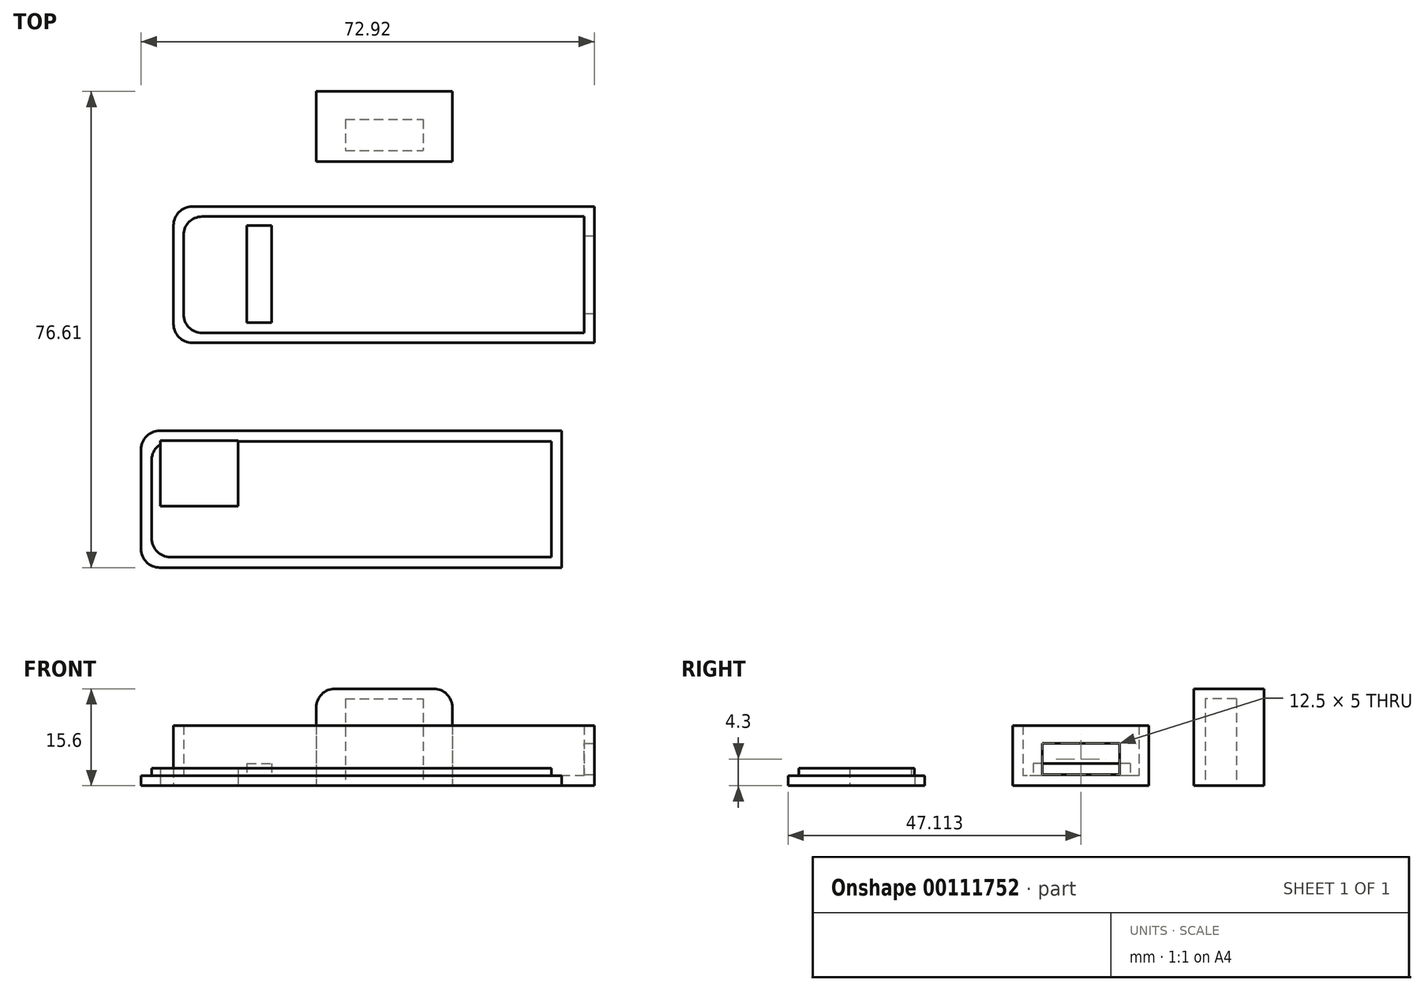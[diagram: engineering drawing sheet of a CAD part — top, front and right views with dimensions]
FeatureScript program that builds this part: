
annotation { "Feature Type Name" : "Feature", "Feature Type Description" : "" }
export const myFeature = defineFeature(function(context is Context, id is Id, definition is map)
    precondition{}
    {
        {
            var Q0;
            Q0=qCreatedBy(makeId("Top.planeOp"),FACE);
            var sketch = newSketch(context, id + "F0", { "sketchPlane" : qUnion([Q0])});
            skLineSegment(sketch, "E0.bottom", {"start": v(32.32, 10.9) * mm, "end": v(-29.18, 10.9) * mm});
            skLineSegment(sketch, "E0.top", {"start": v(32.32, -7.8) * mm, "end": v(-29.18, -7.8) * mm});
            skLineSegment(sketch, "E0.left", {"start": v(32.32, 10.9) * mm, "end": v(32.32, -7.8) * mm});
            skLineSegment(sketch, "E0.right", {"start": v(-32.18, 7.9) * mm, "end": v(-32.18, -4.8) * mm});
            skLineSegment(sketch, "E1.0", {"start": v(33.92, 12.5) * mm, "end": v(-30.78, 12.5) * mm});
            skLineSegment(sketch, "E1.1", {"start": v(33.92, 12.5) * mm, "end": v(33.92, -9.4) * mm});
            skLineSegment(sketch, "E1.2", {"start": v(33.92, -9.4) * mm, "end": v(-30.78, -9.4) * mm});
            skLineSegment(sketch, "E1.3", {"start": v(-33.78, 9.5) * mm, "end": v(-33.78, -6.4) * mm});
            skPoint(sketch, "E2.visualSharp", {"position": v(-32.18, 10.9) * mm});
            skArc(sketch, "E2.filletArc", {"start": v(-29.18, 10.9) * mm, "mid": v(-31.3, 10.02) * mm, "end": v(-32.18, 7.9) * mm});
            skPoint(sketch, "E3.visualSharp", {"position": v(-32.18, -7.8) * mm});
            skArc(sketch, "E3.filletArc", {"start": v(-32.18, -4.8) * mm, "mid": v(-31.3, -6.92) * mm, "end": v(-29.18, -7.8) * mm});
            skPoint(sketch, "E4.visualSharp", {"position": v(-33.78, -9.4) * mm});
            skArc(sketch, "E4.filletArc", {"start": v(-33.78, -6.4) * mm, "mid": v(-32.9, -8.52) * mm, "end": v(-30.78, -9.4) * mm});
            skPoint(sketch, "E5.visualSharp", {"position": v(-33.78, 12.5) * mm});
            skArc(sketch, "E5.filletArc", {"start": v(-30.78, 12.5) * mm, "mid": v(-32.9, 11.62) * mm, "end": v(-33.78, 9.5) * mm});
            skSolve(sketch);
        }
        {
            var Q0;
            Q0=makeQuery(id+"F0.imprint","IMPRINT",FACE,{"disambiguationData":[TD([[makeQuery(id+"F0.imprint","IMPRINT",EDGE,{"derivedFrom":sQuery(id+"F0.wireOp",EDGE,"E0.bottom")}),-1.0]])]});
            extrude(context, id + "F1", {"entities" : qUnion([Q0]), "depth" : (10.5 - 0.8) * mm});
        }
        {
            var Q0;
            Q0=makeQuery(id+"F0.imprint","IMPRINT",FACE,{"disambiguationData":[TD([[makeQuery(id+"F0.imprint","IMPRINT",EDGE,{"derivedFrom":sQuery(id+"F0.wireOp",EDGE,"E0.bottom")}),1.0]])]});
            extrude(context, id + "F2", {"entities" : qUnion([Q0]), "operationType" : NewBodyOperationType.ADD, "depth" : 1.6 * mm});
        }
        {
            var Q0;
            Q0=makeQuery(id+"F1.opExtrude","SWEPT_FACE",FACE,{"disambiguationData":[OSD([sQuery(id+"F0.wireOp",EDGE,"E1.1")])]});
            var sketch = newSketch(context, id + "F3", { "sketchPlane" : qUnion([Q0])});
            skLineSegment(sketch, "E6.bottom", {"start": v(-4.7, 6.8) * mm, "end": v(7.8, 6.8) * mm});
            skLineSegment(sketch, "E6.top", {"start": v(-4.7, 1.8) * mm, "end": v(7.8, 1.8) * mm});
            skLineSegment(sketch, "E6.left", {"start": v(-4.7, 6.8) * mm, "end": v(-4.7, 1.8) * mm});
            skLineSegment(sketch, "E6.right", {"start": v(7.8, 6.8) * mm, "end": v(7.8, 1.8) * mm});
            skSolve(sketch);
        }
        {
            var Q0;
            Q0=makeQuery(id+"F3.imprint","IMPRINT",FACE,{"disambiguationData":[TD([[makeQuery(id+"F3.imprint","IMPRINT",EDGE,{"derivedFrom":sQuery(id+"F3.wireOp",EDGE,"E6.bottom")}),-1.0]])]});
            extrude(context, id + "F4", {"entities" : qUnion([Q0]), "operationType" : NewBodyOperationType.REMOVE, "endBound" : BoundingType.UP_TO_NEXT, "oppositeDirection" : true, "depth" : 25 * mm});
        }
        {
            var Q0;
            Q0=makeQuery(id+"F2.opExtrude","CAP_FACE",FACE,{"disambiguationData":[OSD([sQuery(id+"F0.wireOp",EDGE,"E0.bottom"),sQuery(id+"F0.wireOp",EDGE,"E0.top"),sQuery(id+"F0.wireOp",EDGE,"E0.left"),sQuery(id+"F0.wireOp",EDGE,"E0.right")])],"isStart":false});
            var sketch = newSketch(context, id + "F5", { "sketchPlane" : qUnion([Q0])});
            skLineSegment(sketch, "E7.bottom", {"start": v(-21.98, 9.49) * mm, "end": v(-18, 9.49) * mm});
            skLineSegment(sketch, "E7.top", {"start": v(-21.98, -6.15) * mm, "end": v(-18, -6.15) * mm});
            skLineSegment(sketch, "E7.left", {"start": v(-21.98, 9.49) * mm, "end": v(-21.98, -6.15) * mm});
            skLineSegment(sketch, "E7.right", {"start": v(-18, 9.49) * mm, "end": v(-18, -6.15) * mm});
            skSolve(sketch);
        }
        {
            var Q0;
            Q0 = qSketchRegion(id + "F5", true);
            extrude(context, id + "F6", {"entities" : qUnion([Q0]), "operationType" : NewBodyOperationType.ADD, "depth" : 2 * mm});
        }
        {
            var Q0;
            Q0=qCreatedBy(makeId("Top.planeOp"),FACE);
            var sketch = newSketch(context, id + "F7", { "sketchPlane" : qUnion([Q0])});
            skLineSegment(sketch, "E8.bottom", {"start": v(28.7, -23.56) * mm, "end": v(-36, -23.56) * mm});
            skLineSegment(sketch, "E8.top", {"start": v(28.7, -45.56) * mm, "end": v(-36, -45.56) * mm});
            skLineSegment(sketch, "E8.left", {"start": v(28.7, -23.56) * mm, "end": v(28.7, -45.56) * mm});
            skLineSegment(sketch, "E8.right", {"start": v(-39, -26.56) * mm, "end": v(-39, -42.56) * mm});
            skPoint(sketch, "E9.visualSharp", {"position": v(-39, -23.56) * mm});
            skArc(sketch, "E9.filletArc", {"start": v(-36, -23.56) * mm, "mid": v(-38.13, -24.44) * mm, "end": v(-39, -26.56) * mm});
            skPoint(sketch, "E10.visualSharp", {"position": v(-39, -45.56) * mm});
            skArc(sketch, "E10.filletArc", {"start": v(-39, -42.56) * mm, "mid": v(-38.13, -44.68) * mm, "end": v(-36, -45.56) * mm});
            skLineSegment(sketch, "E11.0", {"start": v(-37.3, -28.26) * mm, "end": v(-37.3, -40.86) * mm});
            skLineSegment(sketch, "E11.1", {"start": v(27, -25.26) * mm, "end": v(-34.3, -25.26) * mm});
            skLineSegment(sketch, "E11.2", {"start": v(27, -25.26) * mm, "end": v(27, -43.86) * mm});
            skLineSegment(sketch, "E11.3", {"start": v(27, -43.86) * mm, "end": v(-34.3, -43.86) * mm});
            skPoint(sketch, "E12.visualSharp", {"position": v(-37.3, -25.26) * mm});
            skArc(sketch, "E12.filletArc", {"start": v(-34.3, -25.26) * mm, "mid": v(-36.43, -26.14) * mm, "end": v(-37.3, -28.26) * mm});
            skPoint(sketch, "E13.visualSharp", {"position": v(-37.3, -43.86) * mm});
            skArc(sketch, "E13.filletArc", {"start": v(-37.3, -40.86) * mm, "mid": v(-36.43, -42.98) * mm, "end": v(-34.3, -43.86) * mm});
            skSolve(sketch);
        }
        {
            var Q0;
            Q0=makeQuery(id+"F7.imprint","IMPRINT",FACE,{"disambiguationData":[TD([[makeQuery(id+"F7.imprint","IMPRINT",EDGE,{"derivedFrom":sQuery(id+"F7.wireOp",EDGE,"E11.0")}),1.0]])]});
            var Q1;
            Q1=makeQuery(id+"F7.imprint","IMPRINT",FACE,{"disambiguationData":[TD([[makeQuery(id+"F7.imprint","IMPRINT",EDGE,{"derivedFrom":sQuery(id+"F7.wireOp",EDGE,"E8.bottom")}),1.0]])]});
            extrude(context, id + "F8", {"entities" : qUnion([Q0, Q1]), "depth" : 1.6 * mm});
        }
        {
            var Q0;
            Q0=makeQuery(id+"F7.imprint","IMPRINT",FACE,{"disambiguationData":[TD([[makeQuery(id+"F7.imprint","IMPRINT",EDGE,{"derivedFrom":sQuery(id+"F7.wireOp",EDGE,"E11.0")}),1.0]])]});
            extrude(context, id + "F9", {"entities" : qUnion([Q0]), "operationType" : NewBodyOperationType.ADD, "depth" : (1.6 + 1.2) * mm});
        }
        {
            var Q0;
            Q0=makeQuery(id+"F8.opExtrude","CAP_FACE",FACE,{"disambiguationData":[OSD([sQuery(id+"F7.wireOp",EDGE,"E8.bottom"),sQuery(id+"F7.wireOp",EDGE,"E8.top"),sQuery(id+"F7.wireOp",EDGE,"E8.left"),sQuery(id+"F7.wireOp",EDGE,"E8.right"),sQuery(id+"F7.wireOp",EDGE,"E9.filletArc"),sQuery(id+"F7.wireOp",EDGE,"E10.filletArc")])],"isStart":true});
            var sketch = newSketch(context, id + "F10", { "sketchPlane" : qUnion([Q0])});
            skLineSegment(sketch, "E14.bottom", {"start": v(-35.9, 35.66) * mm, "end": v(-23.4, 35.66) * mm});
            skLineSegment(sketch, "E14.top", {"start": v(-35.9, 25.16) * mm, "end": v(-23.4, 25.16) * mm});
            skLineSegment(sketch, "E14.left", {"start": v(-35.9, 35.66) * mm, "end": v(-35.9, 25.16) * mm});
            skLineSegment(sketch, "E14.right", {"start": v(-23.4, 35.66) * mm, "end": v(-23.4, 25.16) * mm});
            skSolve(sketch);
        }
        {
            var Q0;
            Q0=makeQuery(id+"F10.imprint","IMPRINT",FACE,{"disambiguationData":[TD([[makeQuery(id+"F10.imprint","IMPRINT",EDGE,{"derivedFrom":sQuery(id+"F10.wireOp",EDGE,"E14.bottom")}),-1.0]])]});
            extrude(context, id + "F11", {"entities" : qUnion([Q0]), "operationType" : NewBodyOperationType.REMOVE, "endBound" : BoundingType.THROUGH_ALL, "oppositeDirection" : true, "depth" : 25 * mm});
        }
        {
            var Q0;
            Q0=qCreatedBy(makeId("Top.planeOp"),FACE);
            var sketch = newSketch(context, id + "F12", { "sketchPlane" : qUnion([Q0])});
            skLineSegment(sketch, "E15.bottom", {"start": v(-10.82, 31.05) * mm, "end": v(11.08, 31.05) * mm});
            skLineSegment(sketch, "E15.top", {"start": v(-10.82, 19.75) * mm, "end": v(11.08, 19.75) * mm});
            skLineSegment(sketch, "E15.left", {"start": v(-10.82, 31.05) * mm, "end": v(-10.82, 19.75) * mm});
            skLineSegment(sketch, "E15.right", {"start": v(11.08, 31.05) * mm, "end": v(11.08, 19.75) * mm});
            skLineSegment(sketch, "E16.bottom", {"start": v(-6.12, 26.55) * mm, "end": v(6.38, 26.55) * mm});
            skLineSegment(sketch, "E16.top", {"start": v(-6.12, 21.55) * mm, "end": v(6.38, 21.55) * mm});
            skLineSegment(sketch, "E16.left", {"start": v(-6.12, 26.55) * mm, "end": v(-6.12, 21.55) * mm});
            skLineSegment(sketch, "E16.right", {"start": v(6.38, 26.55) * mm, "end": v(6.38, 21.55) * mm});
            skSolve(sketch);
        }
        {
            var Q0;
            Q0=makeQuery(id+"F12.imprint","IMPRINT",FACE,{"disambiguationData":[TD([[makeQuery(id+"F12.imprint","IMPRINT",EDGE,{"derivedFrom":sQuery(id+"F12.wireOp",EDGE,"E15.bottom")}),-1.0]])]});
            extrude(context, id + "F13", {"entities" : qUnion([Q0]), "depth" : 14 * mm});
        }
        {
            var Q0;
            Q0=makeQuery(id+"F13.opExtrude","CAP_FACE",FACE,{"disambiguationData":[OSD([sQuery(id+"F12.wireOp",EDGE,"E15.bottom"),sQuery(id+"F12.wireOp",EDGE,"E15.top"),sQuery(id+"F12.wireOp",EDGE,"E15.left"),sQuery(id+"F12.wireOp",EDGE,"E15.right"),sQuery(id+"F12.wireOp",EDGE,"E16.bottom"),sQuery(id+"F12.wireOp",EDGE,"E16.top"),sQuery(id+"F12.wireOp",EDGE,"E16.left"),sQuery(id+"F12.wireOp",EDGE,"E16.right")])],"isStart":false});
            var sketch = newSketch(context, id + "F14", { "sketchPlane" : qUnion([Q0])});
            skLineSegment(sketch, "E17.bottom", {"start": v(-10.82, 31.05) * mm, "end": v(11.08, 31.05) * mm});
            skLineSegment(sketch, "E17.top", {"start": v(-10.82, 19.75) * mm, "end": v(11.08, 19.75) * mm});
            skLineSegment(sketch, "E17.left", {"start": v(-10.82, 31.05) * mm, "end": v(-10.82, 19.75) * mm});
            skLineSegment(sketch, "E17.right", {"start": v(11.08, 31.05) * mm, "end": v(11.08, 19.75) * mm});
            skSolve(sketch);
        }
        {
            var Q0;
            Q0 = qSketchRegion(id + "F14", true);
            extrude(context, id + "F15", {"entities" : qUnion([Q0]), "operationType" : NewBodyOperationType.ADD, "depth" : 1.6 * mm});
        }
        {
            var Q0;
            Q0=makeQuery(id+"F15.opExtrude","CAP_EDGE",EDGE,{"disambiguationData":[OSD([sQuery(id+"F14.wireOp",EDGE,"E17.right")])],"isStart":false});
            var Q1;
            Q1=makeQuery(id+"F15.opExtrude","CAP_EDGE",EDGE,{"disambiguationData":[OSD([sQuery(id+"F14.wireOp",EDGE,"E17.left")])],"isStart":false});
            fillet(context, id + "F16", {"entities" : qUnion([Q0, Q1]), "radius" : 3 * mm, "tangentPropagation" : true, "allowEdgeOverflow" : false});
        }
    });
